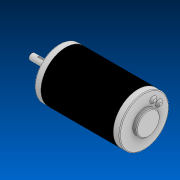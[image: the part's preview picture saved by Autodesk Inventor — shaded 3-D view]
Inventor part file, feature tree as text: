
AUTODESK INVENTOR PART (.ipt)
format: ipt  version: 2022.2 (Build 262287000, 287)  size: 163,840 bytes
history: native  units: in
note: dims shown in document units (in); Inventor stores cm internally (conversion verified against a paired STEP export)
features: chamfer x1
ambient origin geometry x8: Origin, YZ Plane, XZ Plane, XY Plane, X Axis, Y Axis, Z Axis, Center Point
bodies: Solid1 (feature_tree)
feature tree (1):
  chamfer  "Chamfer3"  [1 undecoded]
note: 1 required parameter value undecoded (feature->parameter linkage not recoverable at this tier; creation-order binding heuristic only, values carry confidence <= 0.55)
